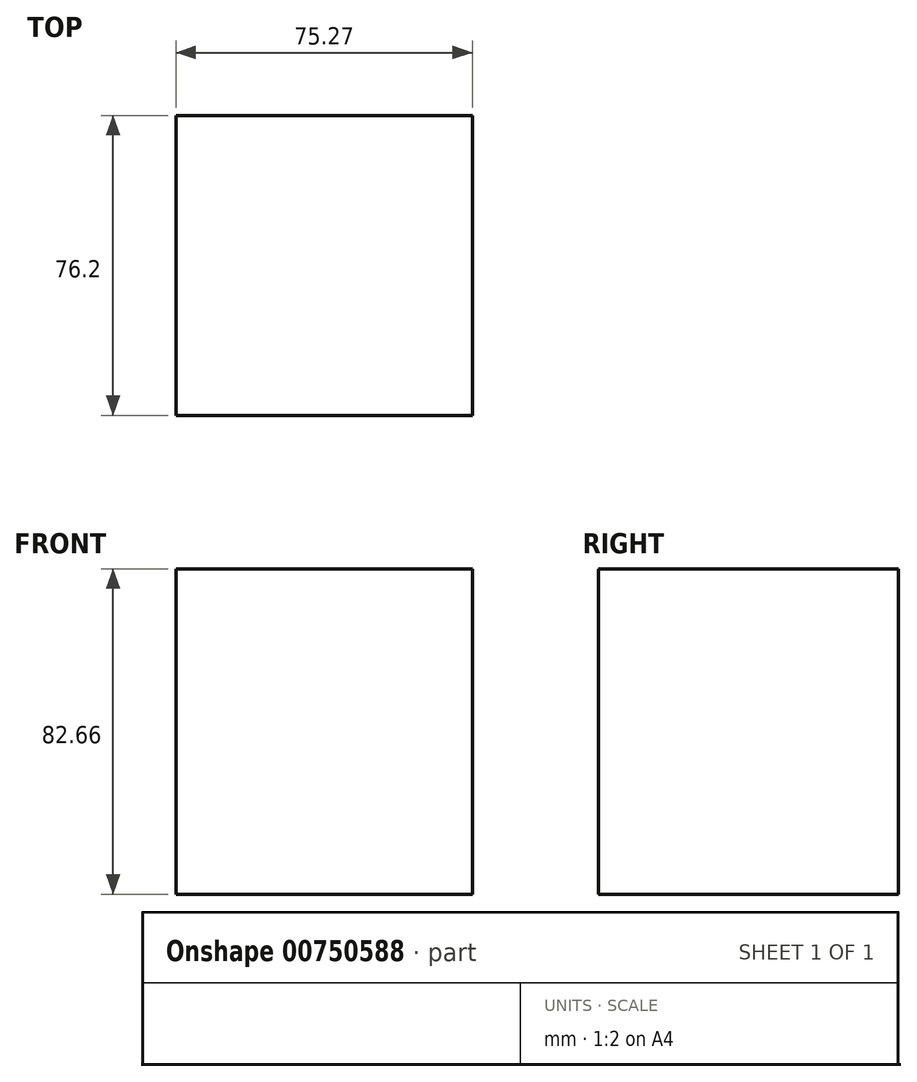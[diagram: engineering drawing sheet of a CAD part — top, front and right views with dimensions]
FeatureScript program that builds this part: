
annotation { "Feature Type Name" : "Feature", "Feature Type Description" : "" }
export const myFeature = defineFeature(function(context is Context, id is Id, definition is map)
    precondition{}
    {
        {
            var Q0;
            Q0=qCreatedBy(makeId("Front.planeOp"),FACE);
            var sketch = newSketch(context, id + "F0", { "sketchPlane" : qUnion([Q0])});
            skLineSegment(sketch, "E0.bottom", {"start": v(-32.14, 44.46) * mm, "end": v(43.13, 44.46) * mm});
            skLineSegment(sketch, "E0.top", {"start": v(-32.14, -38.2) * mm, "end": v(43.13, -38.2) * mm});
            skLineSegment(sketch, "E0.left", {"start": v(-32.14, 44.46) * mm, "end": v(-32.14, -38.2) * mm});
            skLineSegment(sketch, "E0.right", {"start": v(43.13, 44.46) * mm, "end": v(43.13, -38.2) * mm});
            skSolve(sketch);
        }
        {
            var Q0;
            Q0=makeQuery(id+"F0.imprint","IMPRINT",FACE,{"disambiguationData":[TD([[makeQuery(id+"F0.imprint","IMPRINT",EDGE,{"derivedFrom":sQuery(id+"F0.wireOp",EDGE,"E0.bottom")}),-1.0]])]});
            extrude(context, id + "F1", {"entities" : qUnion([Q0]), "oppositeDirection" : true, "depth" : 76.2 * mm, "offsetDistance" : 25.4 * mm});
        }
    });
